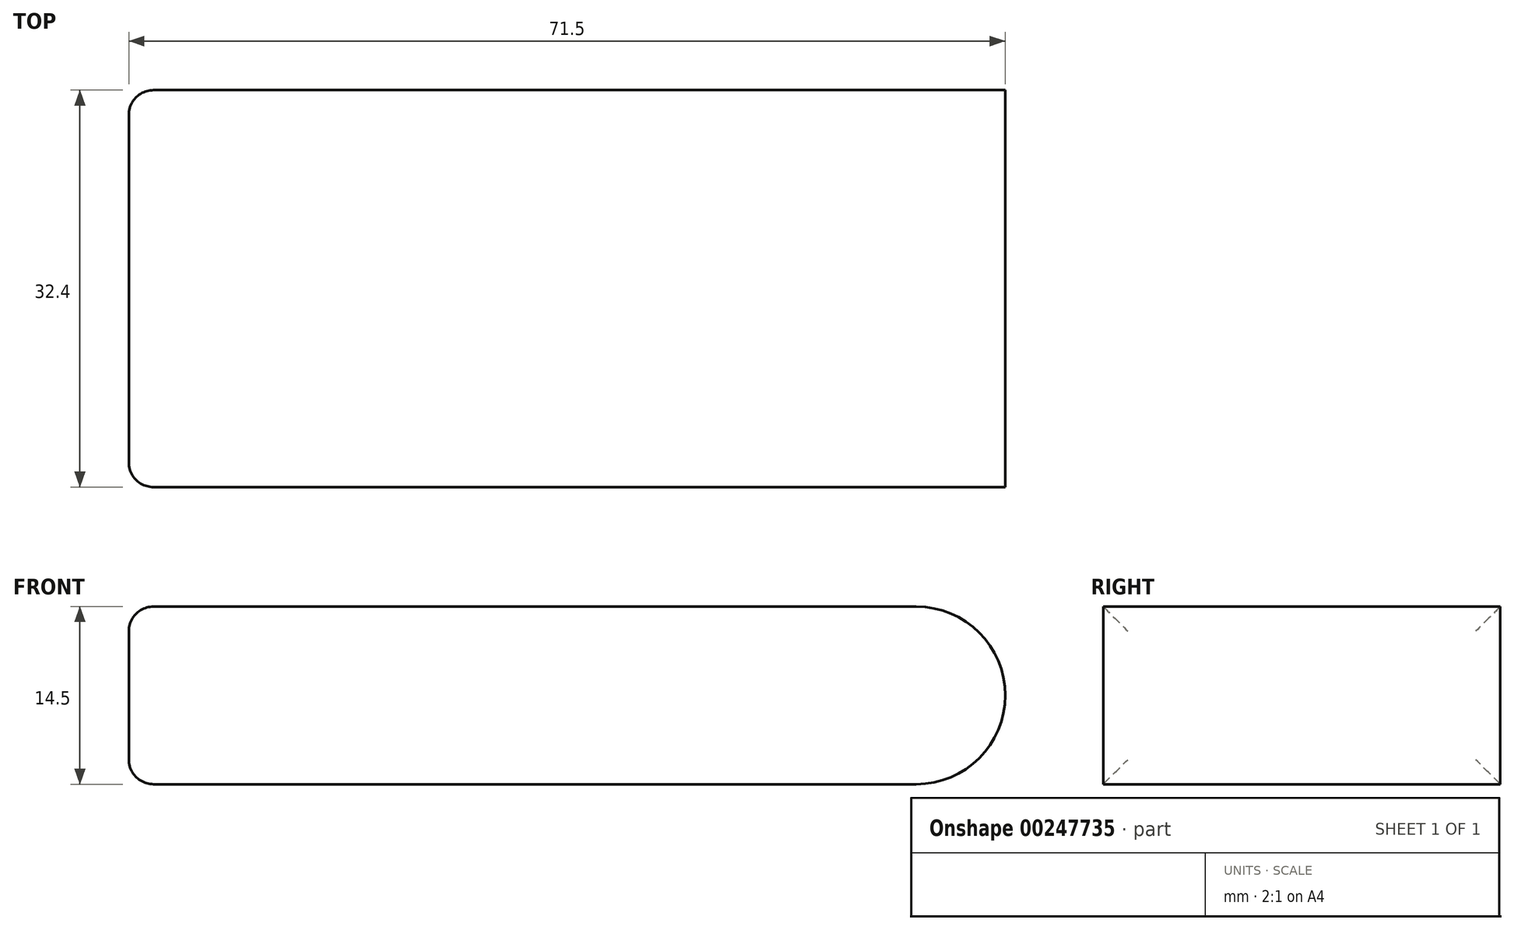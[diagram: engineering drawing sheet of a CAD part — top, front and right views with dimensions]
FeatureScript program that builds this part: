
annotation { "Feature Type Name" : "Feature", "Feature Type Description" : "" }
export const myFeature = defineFeature(function(context is Context, id is Id, definition is map)
    precondition{}
    {
        {
            var Q0;
            Q0=qCreatedBy(makeId("Top.planeOp"),FACE);
            var sketch = newSketch(context, id + "F0", { "sketchPlane" : qUnion([Q0])});
            skLineSegment(sketch, "E0.bottom", {"start": v(-35.75, 16.2) * mm, "end": v(35.75, 16.2) * mm});
            skLineSegment(sketch, "E0.top", {"start": v(-35.75, -16.2) * mm, "end": v(35.75, -16.2) * mm});
            skLineSegment(sketch, "E0.left", {"start": v(-35.75, 16.2) * mm, "end": v(-35.75, -16.2) * mm});
            skLineSegment(sketch, "E0.right", {"start": v(35.75, 16.2) * mm, "end": v(35.75, -16.2) * mm});
            skPoint(sketch, "E0.middle", {"position": v(0, 0) * mm});
            skSolve(sketch);
        }
        {
            var Q0;
            Q0 = qSketchRegion(id + "F0", true);
            extrude(context, id + "F1", {"entities" : qUnion([Q0]), "depth" : 14.5 * mm});
        }
        {
            var Q0;
            Q0=makeQuery(id+"F1.opExtrude","SWEPT_FACE",FACE,{"disambiguationData":[OSD([sQuery(id+"F0.wireOp",EDGE,"E0.left")])]});
            fillet(context, id + "F2", {"entities" : qUnion([Q0]), "radius" : 2 * mm, "tangentPropagation" : true, "allowEdgeOverflow" : false});
        }
        {
            var Q0;
            Q0=makeQuery(id+"F1.opExtrude","CAP_EDGE",EDGE,{"disambiguationData":[OSD([sQuery(id+"F0.wireOp",EDGE,"E0.right")])],"isStart":false});
            var Q1;
            Q1=makeQuery(id+"F1.opExtrude","CAP_EDGE",EDGE,{"disambiguationData":[OSD([sQuery(id+"F0.wireOp",EDGE,"E0.right")])],"isStart":true});
            fillet(context, id + "F3", {"entities" : qUnion([Q0, Q1]), "radius" : 7.25 * mm, "tangentPropagation" : true, "allowEdgeOverflow" : false});
        }
    });
